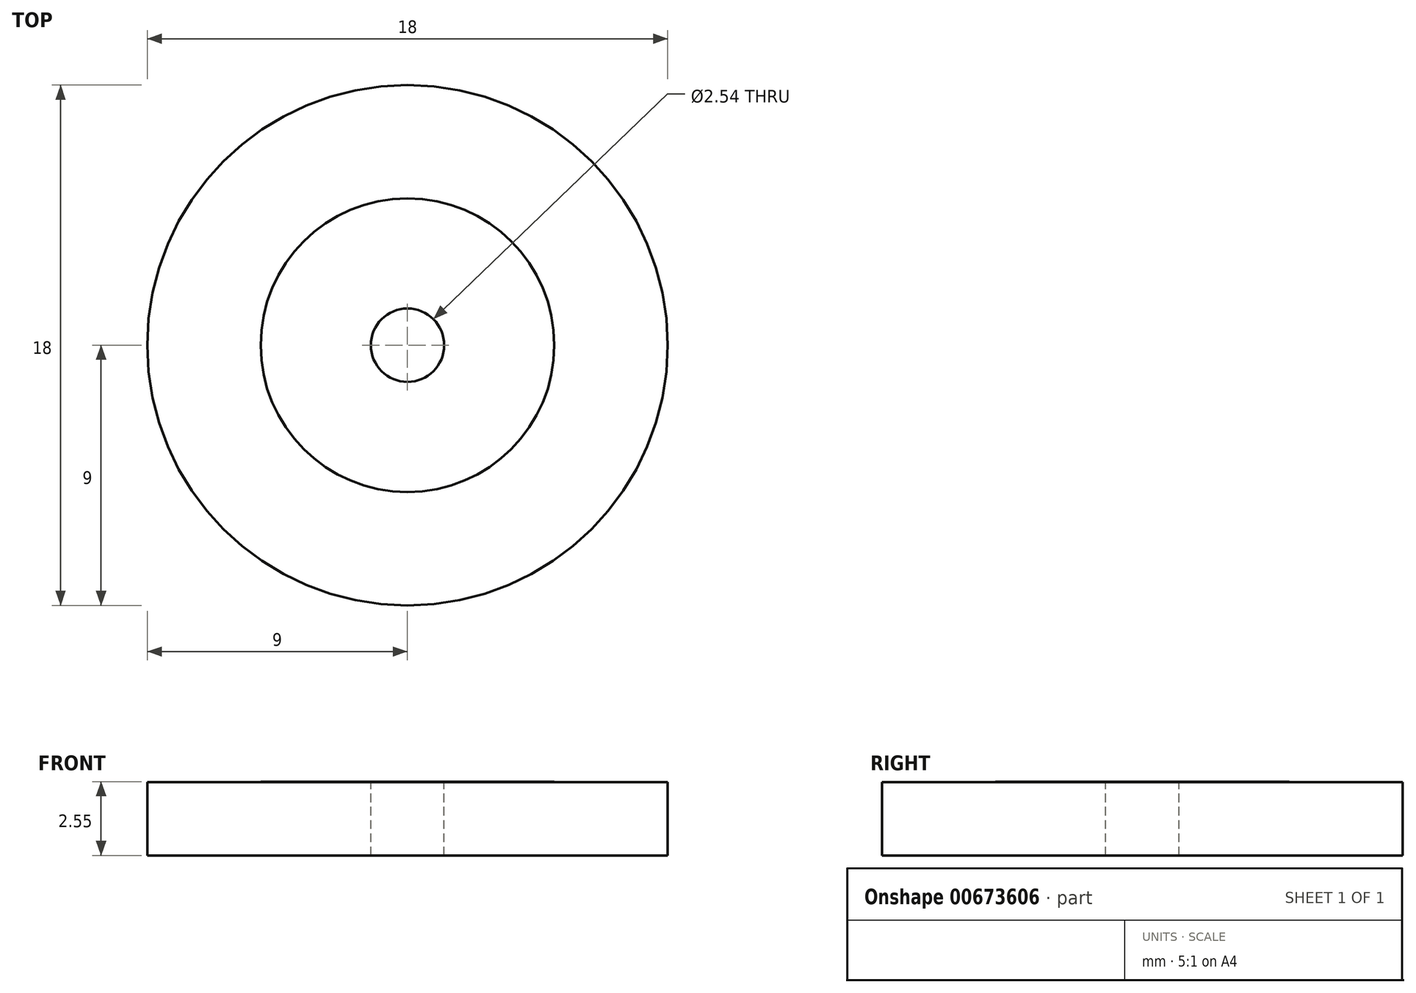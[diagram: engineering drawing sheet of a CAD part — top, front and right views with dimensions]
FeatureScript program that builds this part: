
annotation { "Feature Type Name" : "Feature", "Feature Type Description" : "" }
export const myFeature = defineFeature(function(context is Context, id is Id, definition is map)
    precondition{}
    {
        {
            var Q0;
            Q0=qCreatedBy(makeId("Top.planeOp"),FACE);
            var sketch = newSketch(context, id + "F0", { "sketchPlane" : qUnion([Q0])});
            skCircle(sketch, "E0", {"center": v(0, 0) * mm, "radius": 9 * mm});
            skSolve(sketch);
        }
        {
            var Q0;
            Q0=makeQuery(id+"F0.imprint","IMPRINT",FACE,{"disambiguationData":[TD([[makeQuery(id+"F0.imprint","IMPRINT",EDGE,{"derivedFrom":sQuery(id+"F0.wireOp",EDGE,"E0")}),1.0]])]});
            extrude(context, id + "F1", {"entities" : qUnion([Q0]), "depth" : 2.54 * mm});
        }
        {
            var Q0;
            Q0=makeQuery(id+"F1.opExtrude","CAP_FACE",FACE,{"disambiguationData":[OSD([sQuery(id+"F0.wireOp",EDGE,"E0")])],"isStart":false});
            var sketch = newSketch(context, id + "F2", { "sketchPlane" : qUnion([Q0])});
            skCircle(sketch, "E1", {"center": v(0, 0) * mm, "radius": 5.08 * mm});
            skSolve(sketch);
        }
        {
            var Q0;
            Q0=qSketchRegion(id+"F2",true);
            extrude(context, id + "F3", {"entities" : qUnion([Q0]), "operationType" : NewBodyOperationType.ADD, "depth" : 1 / 177.8 * mm});
        }
        {
            var Q0;
            Q0=makeQuery(id+"F3.opExtrude","CAP_FACE",FACE,{"disambiguationData":[OSD([sQuery(id+"F2.wireOp",EDGE,"E1")])],"isStart":false});
            var sketch = newSketch(context, id + "F4", { "sketchPlane" : qUnion([Q0])});
            skCircle(sketch, "E2", {"center": v(0, 0) * mm, "radius": 1.27 * mm});
            skSolve(sketch);
        }
        {
            var Q0;
            Q0=makeQuery(id+"F4.imprint","IMPRINT",FACE,{"disambiguationData":[TD([[makeQuery(id+"F4.imprint","IMPRINT",EDGE,{"derivedFrom":sQuery(id+"F4.wireOp",EDGE,"E2")}),1.0]])]});
            extrude(context, id + "F5", {"entities" : qUnion([Q0]), "operationType" : NewBodyOperationType.REMOVE, "oppositeDirection" : true, "depth" : 3.63 * mm});
        }
    });
